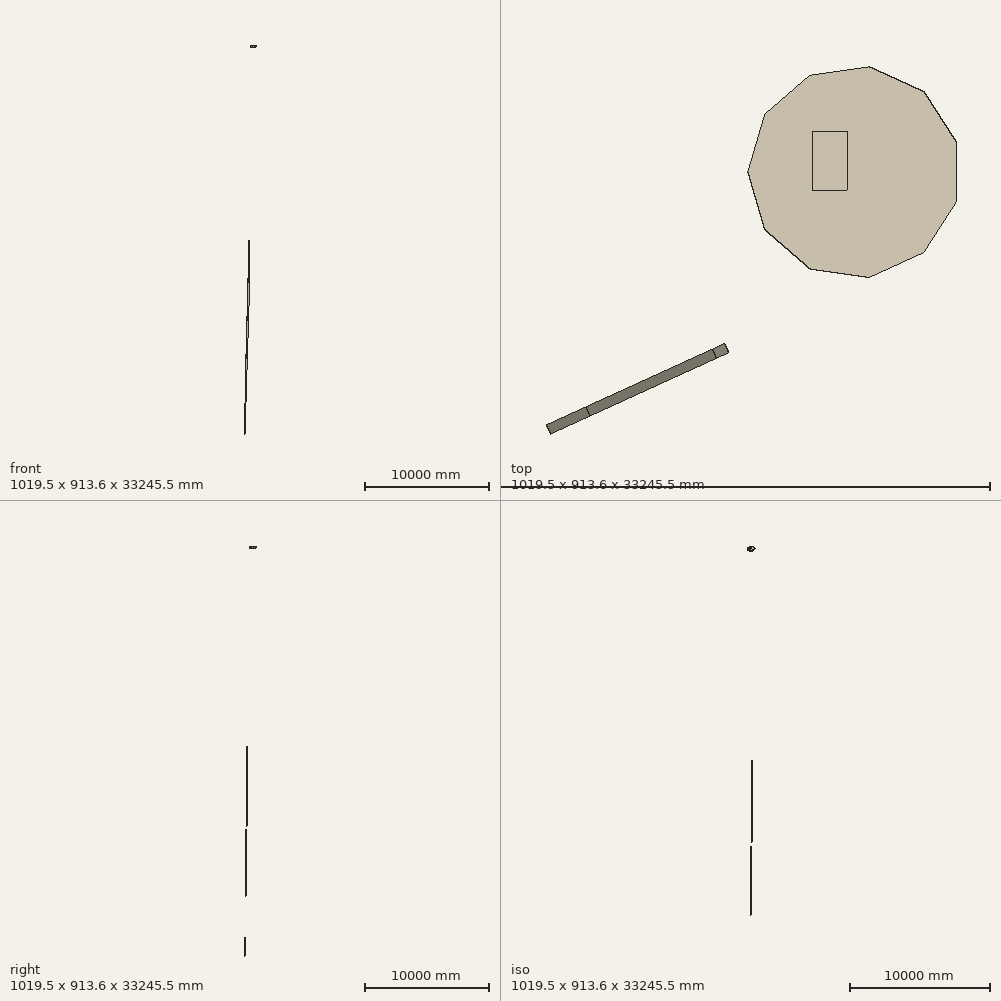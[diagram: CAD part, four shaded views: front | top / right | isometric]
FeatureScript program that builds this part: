
annotation { "Feature Type Name" : "Feature", "Feature Type Description" : "" }
export const myFeature = defineFeature(function(context is Context, id is Id, definition is map)
    precondition{}
    {
        {
            var Q0;
            Q0=qCreatedBy(makeId("Top.planeOp"),FACE);
            var sketch = newSketch(context, id + "F0", { "sketchPlane" : qUnion([Q0])});
            skCircle(sketch, "E0.cCircle", {"center": v(0, 0) * mm, "radius": 254 * mm, "construction": true});
            skLineSegment(sketch, "E0.0", {"start": v(173.36, -200.06) * mm, "end": v(37.67, -262.03) * mm});
            skLineSegment(sketch, "E0.1", {"start": v(37.67, -262.03) * mm, "end": v(-109.97, -240.8) * mm});
            skLineSegment(sketch, "E0.2", {"start": v(-109.97, -240.8) * mm, "end": v(-222.7, -143.12) * mm});
            skLineSegment(sketch, "E0.3", {"start": v(-222.7, -143.12) * mm, "end": v(-264.72, 0) * mm});
            skLineSegment(sketch, "E0.4", {"start": v(-264.72, 0) * mm, "end": v(-222.7, 143.12) * mm});
            skLineSegment(sketch, "E0.5", {"start": v(-222.7, 143.12) * mm, "end": v(-109.97, 240.8) * mm});
            skLineSegment(sketch, "E0.6", {"start": v(-109.97, 240.8) * mm, "end": v(37.67, 262.03) * mm});
            skLineSegment(sketch, "E0.7", {"start": v(37.67, 262.03) * mm, "end": v(173.36, 200.06) * mm});
            skLineSegment(sketch, "E0.8", {"start": v(173.36, 200.06) * mm, "end": v(254, 74.58) * mm});
            skLineSegment(sketch, "E0.9", {"start": v(254, 74.58) * mm, "end": v(254, -74.58) * mm});
            skLineSegment(sketch, "E0.10", {"start": v(254, -74.58) * mm, "end": v(173.36, -200.06) * mm});
            skPoint(sketch, "E0.0.midPoint", {"position": v(105.52, -231.05) * mm});
            skSolve(sketch);
        }
        {
            var Q0;
            Q0 = qSketchRegion(id + "F0", true);
            extrude(context, id + "F1", {"entities" : qUnion([Q0]), "depth" : 100 * mm});
        }
        {
            var Q0;
            Q0=makeQuery(id+"F1.opExtrude","SWEPT_FACE",FACE,{"disambiguationData":[OSD([sQuery(id+"F0.wireOp",EDGE,"E0.0")])]});
            var sketch = newSketch(context, id + "F2", { "sketchPlane" : qUnion([Q0])});
            skLineSegment(sketch, "E1", {"start": v(-470.5, -18956.31) * mm, "end": v(-957.52, -33120.5) * mm});
            skLineSegment(sketch, "E2", {"start": v(-957.52, -33120.5) * mm, "end": v(-849.83, -26698.77) * mm});
            skLineSegment(sketch, "E3", {"start": v(-849.83, -26698.77) * mm, "end": v(-504.02, -14775.93) * mm});
            skLineSegment(sketch, "E4", {"start": v(-504.02, -14775.93) * mm, "end": v(-470.5, -18956.31) * mm});
            skSolve(sketch);
        }
        {
            var Q0;
            Q0 = qSketchRegion(id + "F2", true);
            extrude(context, id + "F3", {"entities" : qUnion([Q0]), "depth" : 25 * mm});
        }
        {
            var Q0;
            Q0=makeQuery(id+"F1.opExtrude","CAP_FACE",FACE,{"disambiguationData":[OSD([sQuery(id+"F0.wireOp",EDGE,"E0.0"),sQuery(id+"F0.wireOp",EDGE,"E0.1"),sQuery(id+"F0.wireOp",EDGE,"E0.2"),sQuery(id+"F0.wireOp",EDGE,"E0.3"),sQuery(id+"F0.wireOp",EDGE,"E0.4"),sQuery(id+"F0.wireOp",EDGE,"E0.5"),sQuery(id+"F0.wireOp",EDGE,"E0.6"),sQuery(id+"F0.wireOp",EDGE,"E0.7"),sQuery(id+"F0.wireOp",EDGE,"E0.8"),sQuery(id+"F0.wireOp",EDGE,"E0.9"),sQuery(id+"F0.wireOp",EDGE,"E0.10")])],"isStart":false});
            var sketch = newSketch(context, id + "F4", { "sketchPlane" : qUnion([Q0])});
            skLineSegment(sketch, "E5.bottom", {"start": v(-18.12, 100.57) * mm, "end": v(-103.28, 100.57) * mm});
            skLineSegment(sketch, "E5.top", {"start": v(-18.12, -45.17) * mm, "end": v(-103.28, -45.17) * mm});
            skLineSegment(sketch, "E5.left", {"start": v(-18.12, 100.57) * mm, "end": v(-18.12, -45.17) * mm});
            skLineSegment(sketch, "E5.right", {"start": v(-103.28, 100.57) * mm, "end": v(-103.28, -45.17) * mm});
            skSolve(sketch);
        }
        {
            var Q0;
            Q0 = qSketchRegion(id + "F4", true);
            extrude(context, id + "F5", {"entities" : qUnion([Q0]), "operationType" : NewBodyOperationType.ADD, "depth" : 25 * mm});
        }
    });
